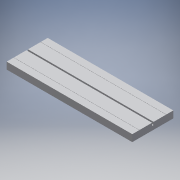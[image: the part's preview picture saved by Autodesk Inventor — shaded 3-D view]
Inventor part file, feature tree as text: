
AUTODESK INVENTOR PART (.ipt)
format: ipt  version: 2018 (Build 220112000, 112)  size: 121,344 bytes
history: native  units: in
note: dims shown in document units (in); Inventor stores cm internally (conversion verified against a paired STEP export)
features: extrude x3, sketch x3
ambient origin geometry x8: Origin, YZ Plane, XZ Plane, XY Plane, X Axis, Y Axis, Z Axis, Center Point
bodies: Solid1 (feature_tree)
feature tree (6):
  extrude  "Extrusion1"  Depth=2.126in
  extrude  "Extrusion2"  Depth=0.0787in
  extrude  "Extrusion3"  Depth=0.0098in
  sketch  "Sketch1"  dims[d0=6.4961in d1=2.126in]
  sketch  "Sketch2"  dims[d2=0.3543in d3=0.0in d4=0.0787in]
  sketch  "Sketch3"  dims[d5=8.0207in d6=0.0in d7=0.689in d8=0.0098in d9=8.0207in d10=0.0in]
